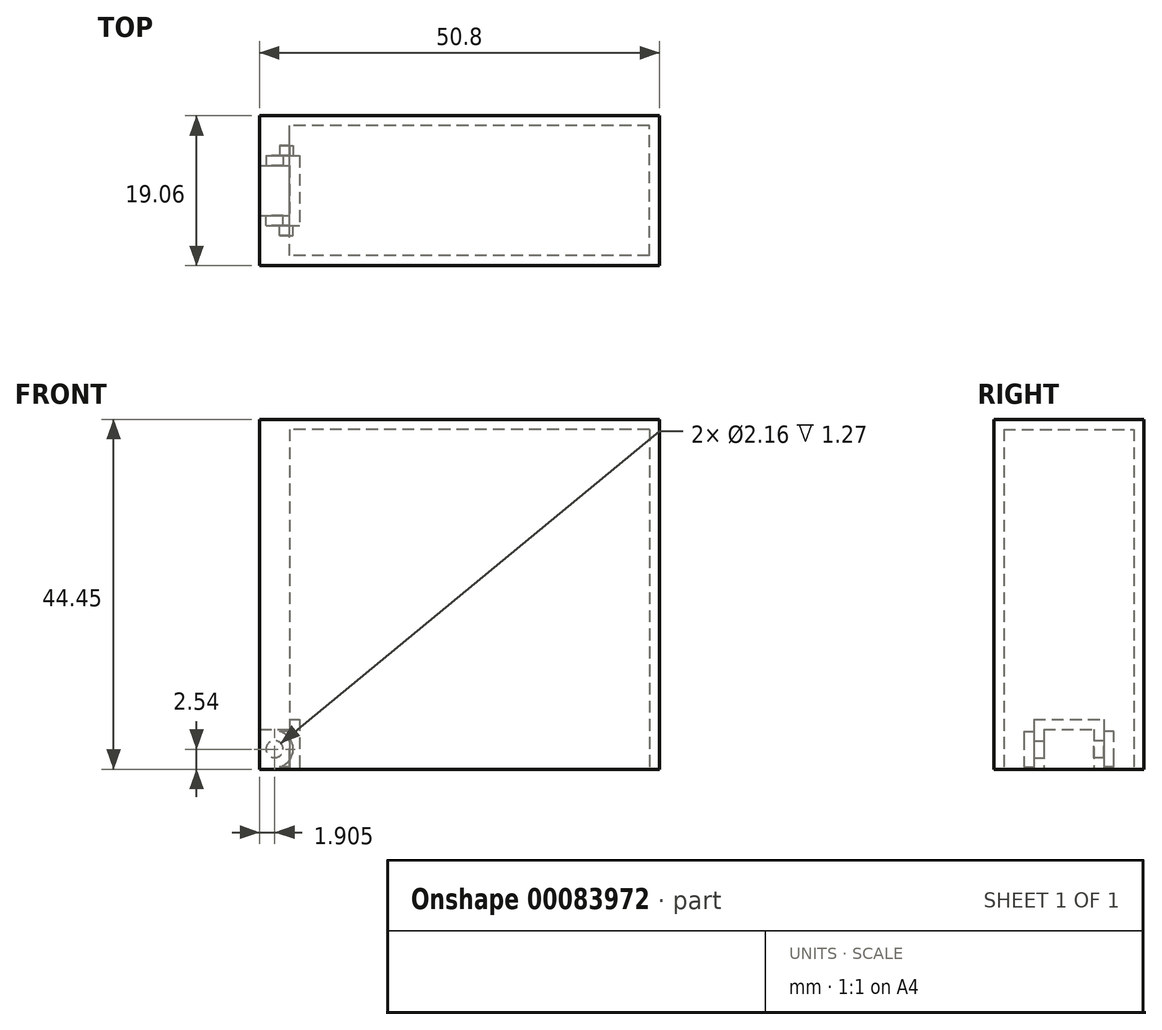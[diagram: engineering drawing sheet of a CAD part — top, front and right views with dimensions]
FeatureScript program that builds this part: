
annotation { "Feature Type Name" : "Feature", "Feature Type Description" : "" }
export const myFeature = defineFeature(function(context is Context, id is Id, definition is map)
    precondition{}
    {
        {
            var Q0;
            Q0=qCreatedBy(makeId("Top.planeOp"),FACE);
            var sketch = newSketch(context, id + "F0", { "sketchPlane" : qUnion([Q0])});
            skLineSegment(sketch, "E0.bottom", {"start": v(25.4, -9.53) * mm, "end": v(-25.4, -9.53) * mm});
            skLineSegment(sketch, "E0.top", {"start": v(25.4, 9.53) * mm, "end": v(-25.4, 9.53) * mm});
            skLineSegment(sketch, "E0.left", {"start": v(25.4, -9.53) * mm, "end": v(25.4, 9.52) * mm});
            skLineSegment(sketch, "E0.right", {"start": v(-25.4, -9.53) * mm, "end": v(-25.4, 9.52) * mm});
            skPoint(sketch, "E0.middle", {"position": v(0, 0) * mm});
            skSolve(sketch);
        }
        {
            var Q0;
            Q0=makeQuery(id+"F0.imprint","IMPRINT",FACE,{"disambiguationData":[TD([[makeQuery(id+"F0.imprint","IMPRINT",EDGE,{"derivedFrom":sQuery(id+"F0.wireOp",EDGE,"E0.bottom")}),-1.0]])]});
            extrude(context, id + "F1", {"entities" : qUnion([Q0]), "depth" : 44.45 * mm});
        }
        {
            var Q0;
            Q0=makeQuery(id+"F1.opExtrude","CAP_FACE",FACE,{"disambiguationData":[OSD([sQuery(id+"F0.wireOp",EDGE,"E0.bottom"),sQuery(id+"F0.wireOp",EDGE,"E0.top"),sQuery(id+"F0.wireOp",EDGE,"E0.left"),sQuery(id+"F0.wireOp",EDGE,"E0.right")])],"isStart":true});
            var sketch = newSketch(context, id + "F2", { "sketchPlane" : qUnion([Q0])});
            skLineSegment(sketch, "E1.bottom", {"start": v(-25.4, -3.18) * mm, "end": v(-21.59, -3.18) * mm});
            skLineSegment(sketch, "E1.top", {"start": v(-25.4, 3.17) * mm, "end": v(-21.59, 3.17) * mm});
            skLineSegment(sketch, "E1.left", {"start": v(-25.4, -3.18) * mm, "end": v(-25.4, 3.17) * mm});
            skLineSegment(sketch, "E1.right", {"start": v(-21.59, -3.18) * mm, "end": v(-21.59, 3.17) * mm});
            skSolve(sketch);
        }
        {
            var Q0;
            Q0 = qSketchRegion(id + "F2", true);
            extrude(context, id + "F3", {"entities" : qUnion([Q0]), "operationType" : NewBodyOperationType.REMOVE, "oppositeDirection" : true, "depth" : 5.08 * mm});
        }
        {
            var Q0;
            Q0=makeQuery(id+"F3.boolean.opBoolean","COPY",FACE,{"derivedFrom":makeQuery(id+"F3.opExtrude","SWEPT_FACE",FACE,{"disambiguationData":[OSD([sQuery(id+"F2.wireOp",EDGE,"E1.bottom")])]})});
            var sketch = newSketch(context, id + "F4", { "sketchPlane" : qUnion([Q0])});
            skCircle(sketch, "E2", {"center": v(-23.5, 2.54) * mm, "radius": 1.08 * mm});
            skSolve(sketch);
        }
        {
            var Q0;
            Q0 = qSketchRegion(id + "F4", true);
            extrude(context, id + "F5", {"entities" : qUnion([Q0]), "operationType" : NewBodyOperationType.REMOVE, "oppositeDirection" : true, "depth" : 1.27 * mm});
        }
        {
            var Q0;
            Q0=makeQuery(id+"F3.boolean.opBoolean","COPY",FACE,{"derivedFrom":makeQuery(id+"F3.opExtrude","SWEPT_FACE",FACE,{"disambiguationData":[OSD([sQuery(id+"F2.wireOp",EDGE,"E1.top")])]})});
            var sketch = newSketch(context, id + "F6", { "sketchPlane" : qUnion([Q0])});
            skCircle(sketch, "E3", {"center": v(23.5, 2.54) * mm, "radius": 1.08 * mm});
            skSolve(sketch);
        }
        {
            var Q0;
            Q0 = qSketchRegion(id + "F6", true);
            extrude(context, id + "F7", {"entities" : qUnion([Q0]), "operationType" : NewBodyOperationType.REMOVE, "oppositeDirection" : true, "depth" : 1.27 * mm});
        }
        {
            var Q0;
            Q0=makeQuery(id+"F1.opExtrude","CAP_FACE",FACE,{"disambiguationData":[OSD([sQuery(id+"F0.wireOp",EDGE,"E0.bottom"),sQuery(id+"F0.wireOp",EDGE,"E0.top"),sQuery(id+"F0.wireOp",EDGE,"E0.left"),sQuery(id+"F0.wireOp",EDGE,"E0.right")])],"isStart":true});
            shell(context, id + "F8", {"entities" : qUnion([Q0]), "thickness" : 1.27 * mm});
        }
        {
            var Q0;
            Q0=makeQuery(id+"F8.opShell","OFFSET_FACE",FACE,{"disambiguationData":[OSD([sQuery(id+"F0.wireOp",EDGE,"E0.right")])]});
            extrude(context, id + "F9", {"entities" : qUnion([Q0]), "operationType" : NewBodyOperationType.ADD, "depth" : 2.54 * mm});
        }
    });
